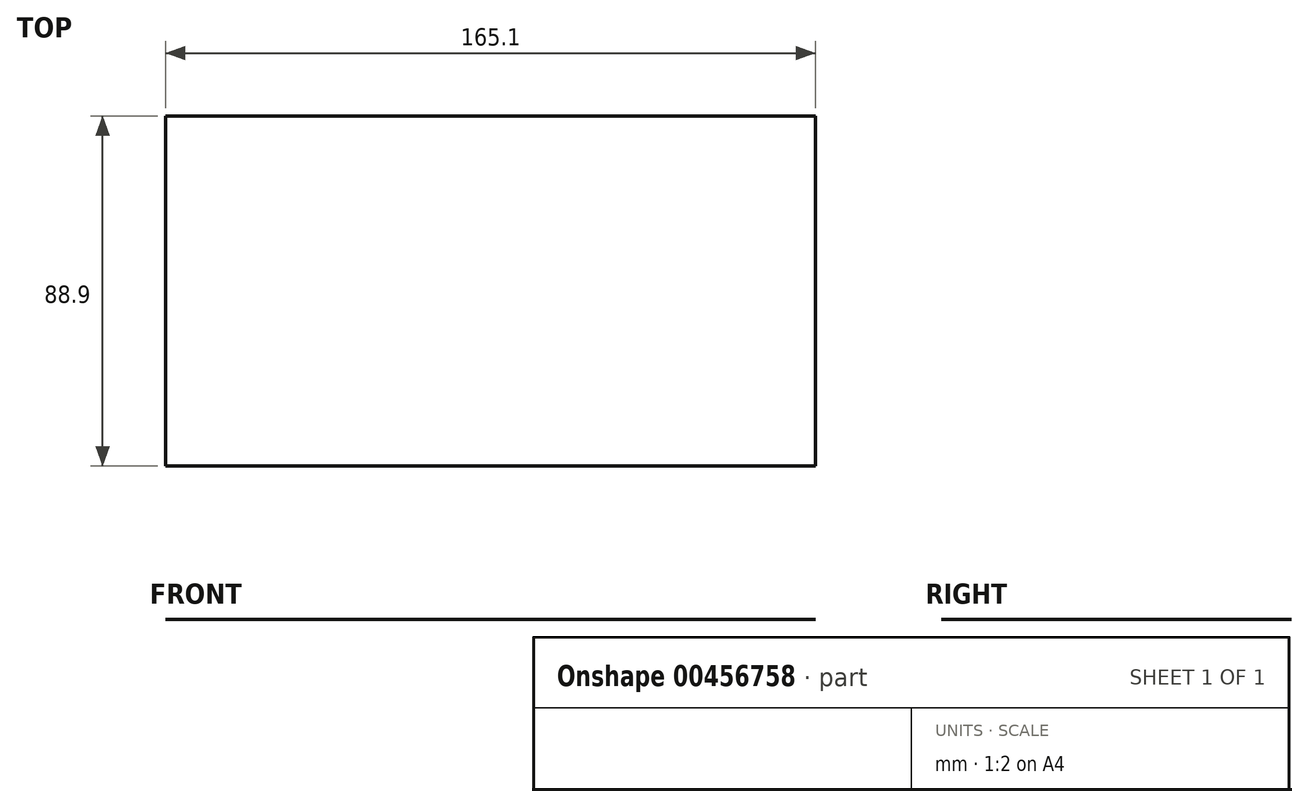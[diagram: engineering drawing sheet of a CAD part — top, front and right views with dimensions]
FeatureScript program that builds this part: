
annotation { "Feature Type Name" : "Feature", "Feature Type Description" : "" }
export const myFeature = defineFeature(function(context is Context, id is Id, definition is map)
    precondition{}
    {
        {
            var Q0;
            Q0=qCreatedBy(makeId("Top.planeOp"),FACE);
            var sketch = newSketch(context, id + "F0", { "sketchPlane" : qUnion([Q0])});
            skLineSegment(sketch, "E0.bottom", {"start": v(-82.55, 44.45) * mm, "end": v(82.55, 44.45) * mm});
            skLineSegment(sketch, "E0.top", {"start": v(-82.55, -44.45) * mm, "end": v(82.55, -44.45) * mm});
            skLineSegment(sketch, "E0.left", {"start": v(-82.55, 44.45) * mm, "end": v(-82.55, -44.45) * mm});
            skLineSegment(sketch, "E0.right", {"start": v(82.55, 44.45) * mm, "end": v(82.55, -44.45) * mm});
            skPoint(sketch, "E0.middle", {"position": v(0, 0) * mm});
            skSolve(sketch);
        }
        {
            var Q0;
            Q0 = qSketchRegion(id + "F0", true);
            extrude(context, id + "F1", {"entities" : qUnion([Q0]), "depth" : 1 / 203.2 * mm});
        }
    });
